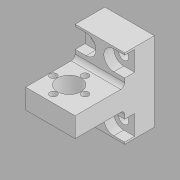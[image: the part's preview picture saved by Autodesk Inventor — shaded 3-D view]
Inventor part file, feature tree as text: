
AUTODESK INVENTOR PART (.ipt)
format: ipt  version: 2020.2 (Build 242310000, 310)  size: 184,832 bytes
history: native  units: mm
features: extrude x4, sketch x4, mirror x2, hole x1, fillet x1
ambient origin geometry x8: Origin, YZ Plane, XZ Plane, XY Plane, X Axis, Y Axis, Z Axis, Center Point
bodies: Solid1 (feature_tree)
feature tree (12):
  extrude  "Extrusion1"  Depth=25.0mm
  hole  "Hole1"  [1 undecoded]
  extrude  "Extrusion3"  Depth=6.0mm
  extrude  "Extrusion4"  Depth=25.0mm
  fillet  "Fillet2"  Radius=25.0mm
  extrude  "Extrusion5"  Depth=25.0mm
  mirror  "Mirror1"
  mirror  "Mirror2"
  sketch  "Sketch1"  dims[d0=40.0mm d1=25.0mm]
  sketch  "Sketch4"  dims[d2=15.0mm d3=0.0mm]
  sketch  "Sketch5"  dims[d9=5.0mm d10=6.0mm d11=10.0mm d12=5.0mm d13=90.0deg d14=8.0mm d15=20.594885mm d20=10.0mm]
  sketch  "Sketch6"  dims[d21=6.0mm d22=6.0mm d24=5.5mm d25=25.0mm d26=0.0mm d27=12.0mm d28=12.0mm d29=15.0mm d30=3.5mm d31=8.0mm d32=40.0mm d34=360.0deg d36=0.0mm d37=0.0mm d38=2.0mm d39=25.0mm d40=0.0mm]
note: 1 required parameter value undecoded (feature->parameter linkage not recoverable at this tier; creation-order binding heuristic only, values carry confidence <= 0.55)
